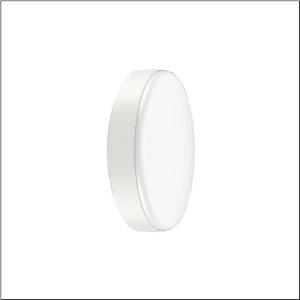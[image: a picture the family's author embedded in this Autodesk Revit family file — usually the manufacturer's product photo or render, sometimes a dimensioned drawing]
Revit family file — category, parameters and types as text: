
# Revit family: rondel_31_51wc10db34as
name_source: partatom
category: Lighting Fixtures
units: mm (PartAtom-declared; Revit-internal decimal feet)

## family parameters
Cut with Voids When Loaded = No
Host = Face
Light Source = No
Part Type = Normal
Room Calculation Point = No
Round Connector Dimension = Use Diameter
Shared = No

## types (1)
- Rondel 31 (1 x LED, 4250 lm, 35.4 W, 3000K)
    Apparent Load = 35 VA
    CIE Flux Codes = 44 75 94 94 100
    Color Rendering = 80
    Color Temperature = 3000K
    Default Elevation = 1800 mm
    Description = Rondel 31, wall and ceiling luminaire, primary optical cover: cover, of PC, opal, light emission: direct distribution, primary light characteristic: symmetric, installation type: surface-mounted, LED, rated luminous flux: 4.250lm, luminous efficacy: 120lm/W, light colour: 830, colour temperature: 3000K, with terminal, 5-pole, max. 2.5mm², mains connection: 220..240V, AC, 50/60Hz, rated input power: 35.5W, luminaire housing, of PC, traffic white (RAL 9016), diameter: 480mm, brightness and presence sensor, HF sensor, protection rating (complete): IP65, insulation class (complete): insulation class II (safety insulation), certification: CE, impact resistance: IK10, permissible operating ambient temperature: -20..+40°C, permissible storage temperature: -20..+60°C, packaging unit: 1 piece
    Height = 97 mm
    Lamp = 1 x LED
    Lamp Light Flux = 4250 lm
    Lamp Power = 35.4 W
    Lamp count = 1
    Length = 480 mm
    Luminous efficacy = 120 lm/W
    Manufacturer = Siteco
    ModVariant = No
    Model = 51WC10DB34AS
    Mounting Place = Ceiling
    Mounting Type = Surface mounted
    Number of Poles = 1
    OnlyDefault = Yes
    Power Factor = 1
    Product Name = Rondel 31
    Product group = wall and ceiling luminaire
    ProductGroupID = 301
    Protection Class = Protection class II
    Protection Degree = IP 65
    RLX_Detail_Level = 1
    RLX_Emergency_Light_Flux = 0 lm
    RLX_Emergency_Type = 0
    RLX_Emergency_Type_DB = No
    RlxData = <blob elided: 40833 chars, md5=bb673235>
    Socket = socket
    Standby Power = 0 W
    System Light Flux = 4250 lm
    System Power = 35 W
    Type Comments = Product without accessories
    Type Image = l_1007188.jpg
    URL = http://relux.com
    VarID = ---
    Voltage = 0 V
    Weight = 0.00 kg
    Width = 0 mm  [stored 0 ft]

note: [stored X ft] marks values corroborated as IEEE doubles in the binary element streams (Revit-internal decimal feet)

## geometry (parser evidence)
native form markers: Blend x4, Sweep x11
no freeform markers — native parametric forms only
